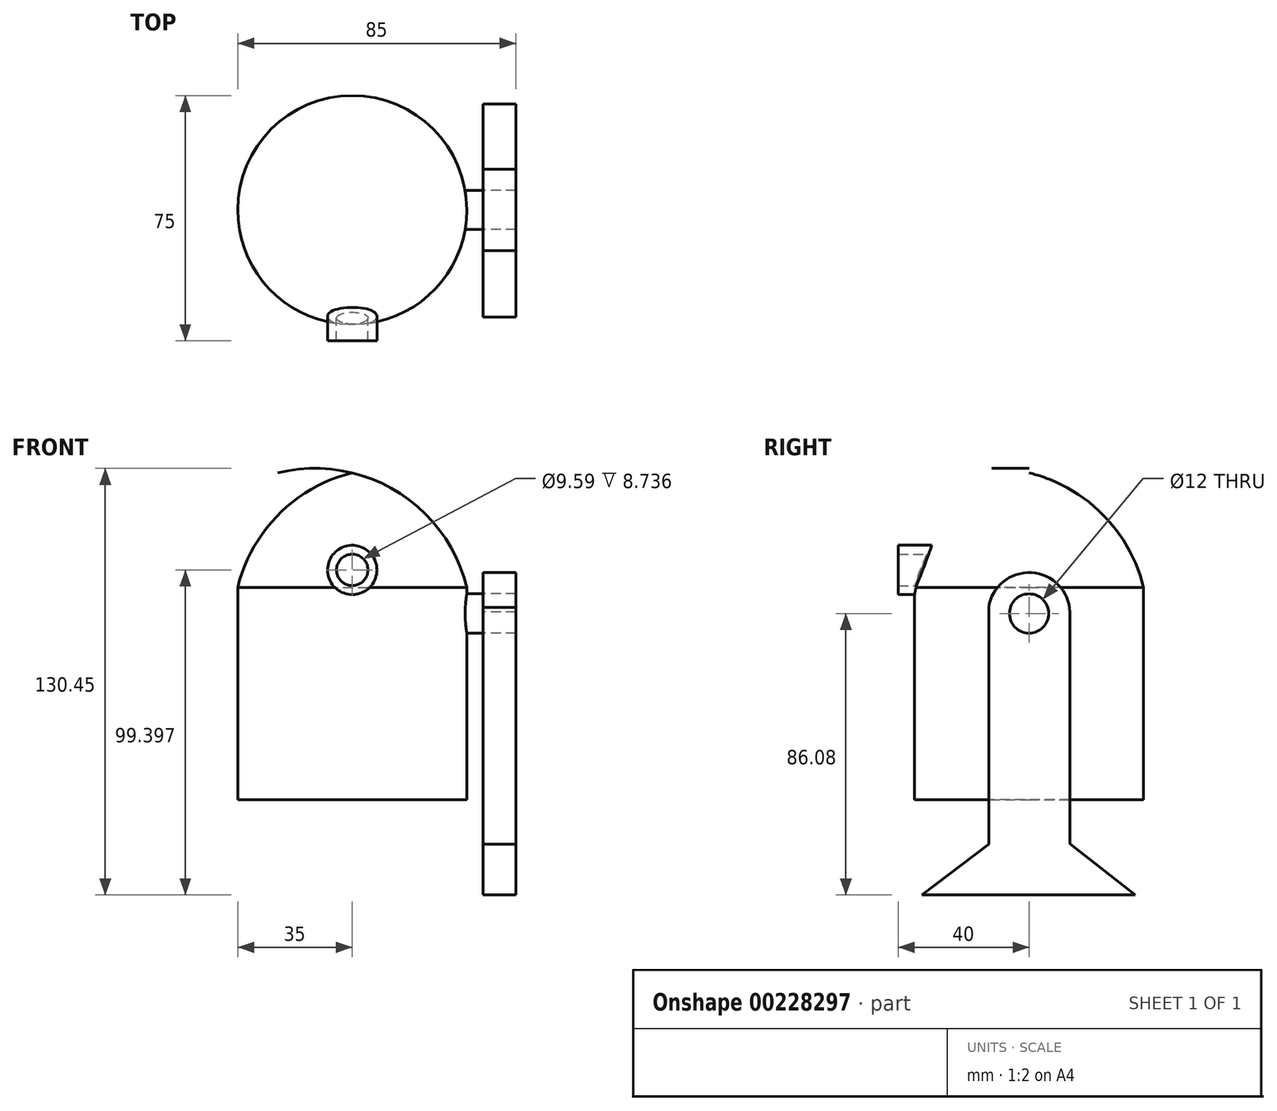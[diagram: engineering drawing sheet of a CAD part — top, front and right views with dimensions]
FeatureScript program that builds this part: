
annotation { "Feature Type Name" : "Feature", "Feature Type Description" : "" }
export const myFeature = defineFeature(function(context is Context, id is Id, definition is map)
    precondition{}
    {
        {
            var Q0;
            Q0=qCreatedBy(makeId("Front.planeOp"),FACE);
            var sketch = newSketch(context, id + "F0", { "sketchPlane" : qUnion([Q0])});
            skLineSegment(sketch, "E0", {"start": v(0, 0) * mm, "end": v(0, 100) * mm});
            skLineSegment(sketch, "E1", {"start": v(0, 0) * mm, "end": v(35, 0) * mm});
            skLineSegment(sketch, "E2", {"start": v(35, 0) * mm, "end": v(35, 65) * mm});
            skArc(sketch, "E3", {"start": v(35, 65) * mm, "mid": v(22.39, 87.39) * mm, "end": v(0, 100) * mm});
            skSolve(sketch);
        }
        {
            var Q0;
            Q0=makeQuery(id+"F0.imprint","IMPRINT",FACE,{"disambiguationData":[TD([[makeQuery(id+"F0.imprint","IMPRINT",EDGE,{"derivedFrom":sQuery(id+"F0.wireOp",EDGE,"E0")}),-1.0]])]});
            var Q1;
            Q1=sQuery(id+"F0.wireOp",EDGE,"E0");
            revolve(context, id + "F1", {"entities" : qUnion([Q0]), "axis" : qUnion([Q1]), "revolveType" : RevolveType.FULL});
        }
        {
            var Q0;
            Q0=qCreatedBy(makeId("Right.planeOp"),FACE);
            var sketch = newSketch(context, id + "F2", { "sketchPlane" : qUnion([Q0])});
            skCircle(sketch, "E4", {"center": v(0, 57) * mm, "radius": 6 * mm});
            skSolve(sketch);
        }
        {
            var Q0;
            Q0 = qSketchRegion(id + "F2", true);
            extrude(context, id + "F3", {"entities" : qUnion([Q0]), "operationType" : NewBodyOperationType.ADD, "depth" : 40 * mm});
        }
        {
            var Q0;
            Q0=makeQuery(id+"F3.opExtrude","CAP_FACE",FACE,{"disambiguationData":[OSD([sQuery(id+"F2.wireOp",EDGE,"E4")])],"isStart":false});
            var sketch = newSketch(context, id + "F4", { "sketchPlane" : qUnion([Q0])});
            skArc(sketch, "E5", {"start": v(12.5, 56.59) * mm, "mid": v(-0.71, 69.48) * mm, "end": v(-12.37, 55.17) * mm});
            skLineSegment(sketch, "E6", {"start": v(12.5, 57.41) * mm, "end": v(12.5, -13.46) * mm});
            skLineSegment(sketch, "E7", {"start": v(12.5, -13.46) * mm, "end": v(32.4, -29.08) * mm});
            skLineSegment(sketch, "E8", {"start": v(32.4, -29.08) * mm, "end": v(-17.03, -29.08) * mm});
            skLineSegment(sketch, "E9", {"start": v(-12.37, 58.83) * mm, "end": v(-12.37, -13.5) * mm});
            skLineSegment(sketch, "E10", {"start": v(-17.03, -29.08) * mm, "end": v(-32.68, -29.08) * mm});
            skLineSegment(sketch, "E11", {"start": v(-32.68, -29.08) * mm, "end": v(-12.37, -13.5) * mm});
            skSolve(sketch);
        }
        {
            var Q0;
            {var subQ3=sQuery(id+"F4.wireOp",EDGE,"E7");Q0=makeQuery(id+"F4.imprint","IMPRINT",FACE,{"disambiguationData":[TD([[makeQuery(id+"F4.imprint","IMPRINT",EDGE,{"derivedFrom":subQ3}),-1.0]])]});}
            extrude(context, id + "F5", {"entities" : qUnion([Q0]), "depth" : 10 * mm});
        }
        {
            var Q0;
            Q0=qCreatedBy(makeId("Front.planeOp"),FACE);
            var sketch = newSketch(context, id + "F6", { "sketchPlane" : qUnion([Q0])});
            skCircle(sketch, "E12", {"center": v(0, 86.13) * mm, "radius": 7.5 * mm});
            skSolve(sketch);
        }
        {
            var Q0;
            Q0 = qSketchRegion(id + "F6", true);
            extrude(context, id + "F7", {"entities" : qUnion([Q0]), "operationType" : NewBodyOperationType.ADD, "depth" : 30 * mm});
        }
        {
            var Q0;
            Q0=qCreatedBy(makeId("Front.planeOp"),FACE);
            var sketch = newSketch(context, id + "F8", { "sketchPlane" : qUnion([Q0])});
            skCircle(sketch, "E13", {"center": v(0, 70.32) * mm, "radius": 4.8 * mm});
            skCircle(sketch, "E14", {"center": v(0, 70.32) * mm, "radius": 7.53 * mm});
            skSolve(sketch);
        }
        {
            var Q0;
            Q0 = qSketchRegion(id + "F8", true);
            extrude(context, id + "F9", {"entities" : qUnion([Q0]), "operationType" : NewBodyOperationType.ADD, "depth" : 40 * mm});
        }
    });
